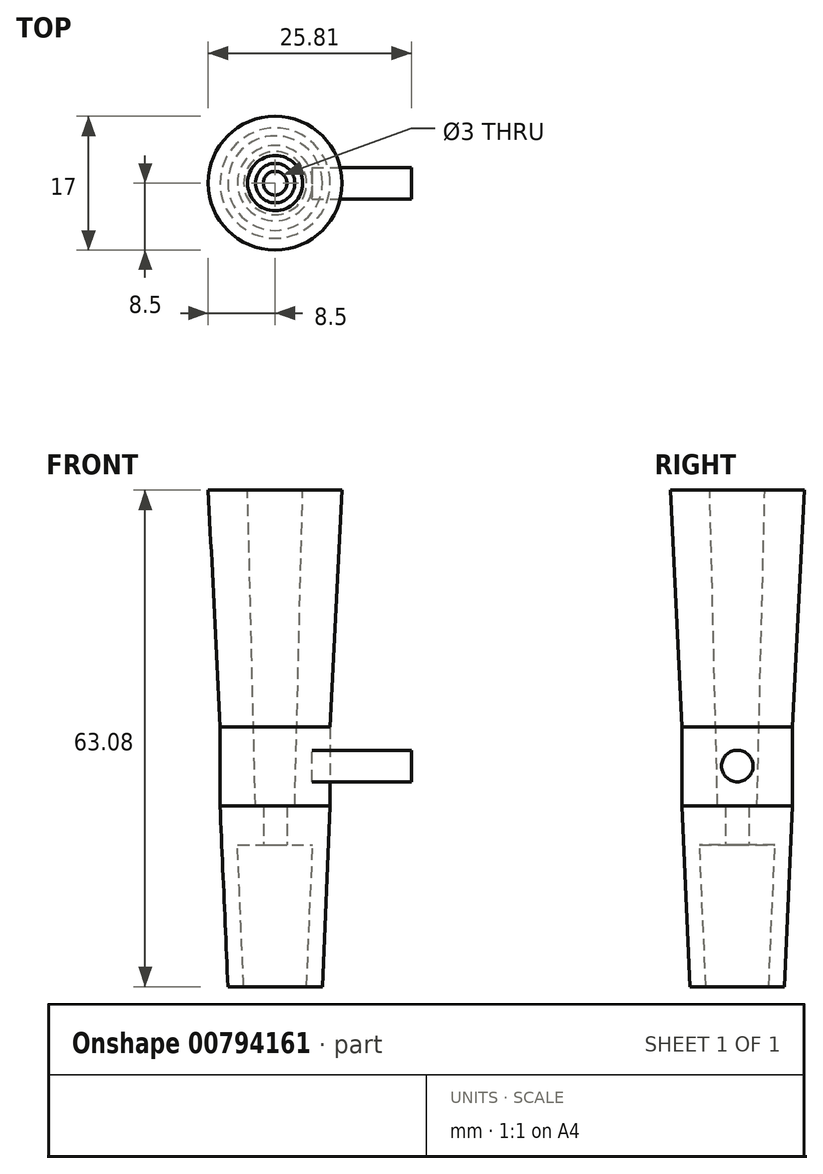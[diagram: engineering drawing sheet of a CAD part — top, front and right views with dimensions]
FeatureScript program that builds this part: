
annotation { "Feature Type Name" : "Feature", "Feature Type Description" : "" }
export const myFeature = defineFeature(function(context is Context, id is Id, definition is map)
    precondition{}
    {
        {
            var Q0;
            Q0=qCreatedBy(makeId("Front.planeOp"),FACE);
            var sketch = newSketch(context, id + "F0", { "sketchPlane" : qUnion([Q0])});
            skLineSegment(sketch, "E0", {"start": v(0, 0) * mm, "end": v(0, -22.98) * mm});
            skLineSegment(sketch, "E1", {"start": v(0, -22.98) * mm, "end": v(6, -22.98) * mm});
            skLineSegment(sketch, "E2", {"start": v(6, -22.98) * mm, "end": v(7, 0) * mm});
            skLineSegment(sketch, "E3", {"start": v(7, 0) * mm, "end": v(0, 0) * mm});
            skLineSegment(sketch, "E4", {"start": v(0, -5) * mm, "end": v(6.78, -5) * mm});
            skLineSegment(sketch, "E5", {"start": v(1.5, 0) * mm, "end": v(1.5, -5) * mm});
            skLineSegment(sketch, "E6", {"start": v(4.78, -5) * mm, "end": v(4, -22.98) * mm});
            skLineSegment(sketch, "E7", {"start": v(7, 0) * mm, "end": v(7, 10) * mm});
            skLineSegment(sketch, "E8", {"start": v(0, 10.1) * mm, "end": v(0, 0) * mm});
            skLineSegment(sketch, "E9", {"start": v(0, 10.1) * mm, "end": v(0, 40.1) * mm});
            skLineSegment(sketch, "E10", {"start": v(0, 40.1) * mm, "end": v(8.5, 40.1) * mm});
            skPoint(sketch, "E11.endSnap0", {"position": v(3.5, 10) * mm});
            skLineSegment(sketch, "E12", {"start": v(7, 10) * mm, "end": v(0, 10.1) * mm});
            skLineSegment(sketch, "E13", {"start": v(8.5, 40.1) * mm, "end": v(7, 10) * mm});
            skLineSegment(sketch, "E14", {"start": v(3.5, 40.1) * mm, "end": v(2.5, 0) * mm});
            skLineSegment(sketch, "E15", {"start": v(0, 5.05) * mm, "end": v(7, 5.05) * mm});
            skPoint(sketch, "E15.endSnap0", {"position": v(7, 5) * mm});
            skLineSegment(sketch, "E16", {"start": v(7, 5.05) * mm, "end": v(2.63, 5.05) * mm});
            skLineSegment(sketch, "E17", {"start": v(4.81, 5.05) * mm, "end": v(17.31, 5.05) * mm});
            skSolve(sketch);
        }
        {
            var Q0;
            {var subQ3=sQuery(id+"F0.wireOp",EDGE,"E13");Q0=makeQuery(id+"F0.imprint","IMPRINT",FACE,{"disambiguationData":[TD([[makeQuery(id+"F0.imprint","IMPRINT",EDGE,{"derivedFrom":subQ3}),-1.0]])]});}
            var Q1;
            {var subQ0=sQuery(id+"F0.wireOp",EDGE,"E5");Q1=makeQuery(id+"F0.imprint","IMPRINT",FACE,{"disambiguationData":[TD([[makeQuery(id+"F0.imprint","IMPRINT",EDGE,{"derivedFrom":subQ0}),1.0]])]});}
            var Q2;
            {var subQ0=sQuery(id+"F0.wireOp",EDGE,"E15");var subQ3=makeQuery(id+"F0.imprint","IMPRINT",VERTEX,{"derivedFrom":subQ0});var subQ4=makeQuery(id+"F0.imprint","IMPRINT",EDGE,{"disambiguationData":[TD([[subQ3,1.0]])],"derivedFrom":subQ0});Q2=qUnion([makeQuery(id+"F0.imprint","IMPRINT",FACE,{"disambiguationData":[TD([[subQ4,-1.0]])]}),makeQuery(id+"F0.imprint","IMPRINT",FACE,{"disambiguationData":[TD([[subQ4,1.0]])]})]);}
            var Q3;
            {var subQ3=sQuery(id+"F0.wireOp",EDGE,"E6");Q3=makeQuery(id+"F0.imprint","IMPRINT",FACE,{"disambiguationData":[TD([[makeQuery(id+"F0.imprint","IMPRINT",EDGE,{"derivedFrom":subQ3}),1.0]])]});}
            var Q4;
            Q4=sQuery(id+"F0.wireOp",EDGE,"E9");
            revolve(context, id + "F1", {"surfaceOperationType" : NewSurfaceOperationType.NEW, "entities" : qUnion([Q0, Q1, Q2, Q3]), "axis" : qUnion([Q4]), "revolveType" : RevolveType.FULL});
        }
        {
            var Q0;
            Q0=sQuery(id+"F0.wireOp",VERTEX,"E17.end");
            var Q1;
            Q1=sQuery(id+"F0.wireOp",EDGE,"E17");
            cPlane(context, id + "F2", {"entities" : qUnion([Q0, Q1]), "cplaneType" : CPlaneType.CURVE_POINT, "offset" : 25 * mm, "width" : 150 * mm, "height" : 150 * mm});
        }
        {
            var Q0;
            Q0=qCreatedBy(id+"F2.planeOp",FACE);
            var sketch = newSketch(context, id + "F3", { "sketchPlane" : qUnion([Q0])});
            skPoint(sketch, "E18.0", {"position": v(0, 5.05) * mm});
            skCircle(sketch, "E19", {"center": v(0, 5.05) * mm, "radius": 2 * mm});
            skSolve(sketch);
        }
        {
            var Q0;
            Q0=makeQuery(id+"F3.imprint","IMPRINT",FACE,{"disambiguationData":[TD([[makeQuery(id+"F3.imprint","IMPRINT",EDGE,{"derivedFrom":sQuery(id+"F3.wireOp",EDGE,"E19")}),1.0]])]});
            extrude(context, id + "F4", {"entities" : qUnion([Q0]), "oppositeDirection" : true, "depth" : 12.66 * mm, "offsetDistance" : 25 * mm});
        }
    });
